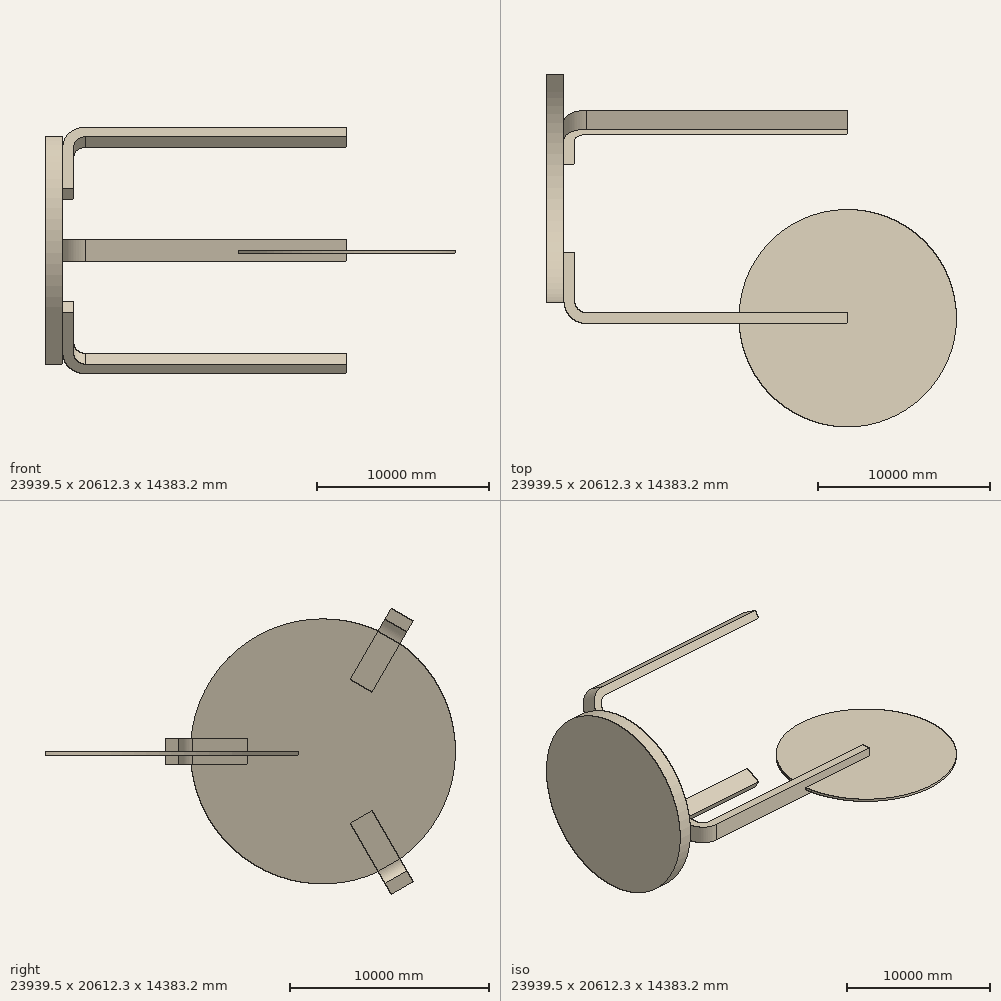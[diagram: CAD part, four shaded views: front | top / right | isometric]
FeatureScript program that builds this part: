
annotation { "Feature Type Name" : "Feature", "Feature Type Description" : "" }
export const myFeature = defineFeature(function(context is Context, id is Id, definition is map)
    precondition{}
    {
        {
            var Q0;
            Q0=qCreatedBy(makeId("Top.planeOp"),FACE);
            var sketch = newSketch(context, id + "F0", { "sketchPlane" : qUnion([Q0])});
            skCircle(sketch, "E0", {"center": v(0, 0) * mm, "radius": 6350 * mm});
            skSolve(sketch);
        }
        {
            var Q0;
            Q0 = qSketchRegion(id + "F0", true);
            extrude(context, id + "F1", {"entities" : qUnion([Q0]), "oppositeDirection" : true, "depth" : 177.8 * mm, "offsetDistance" : 25.4 * mm});
        }
        {
            var Q0;
            Q0=makeQuery(id+"F1.opExtrude","CAP_EDGE",EDGE,{"disambiguationData":[OSD([sQuery(id+"F0.wireOp",EDGE,"E0")])],"isStart":true});
            cPlane(context, id + "F2", {"entities" : qUnion([Q0]), "cplaneType" : CPlaneType.LINE_ANGLE, "offset" : 25.4 * mm, "angle" : 0 * degree, "width" : 152.4 * mm, "height" : 152.4 * mm});
        }
        {
            var Q0;
            Q0=qCreatedBy(id+"F2.planeOp",FACE);
            var sketch = newSketch(context, id + "F3", { "sketchPlane" : qUnion([Q0])});
            skLineSegment(sketch, "E1.bottom", {"start": v(0, 0) * mm, "end": v(1270, 0) * mm});
            skLineSegment(sketch, "E1.top", {"start": v(0, 508) * mm, "end": v(1270, 508) * mm});
            skLineSegment(sketch, "E1.left", {"start": v(0, 0) * mm, "end": v(0, 508) * mm});
            skLineSegment(sketch, "E1.right", {"start": v(1270, 0) * mm, "end": v(1270, 508) * mm});
            skSolve(sketch);
        }
        {
            var Q0;
            Q0=sQuery(id+"F3.wireOp",EDGE,"E1.bottom");
            cPlane(context, id + "F4", {"entities" : qUnion([Q0]), "cplaneType" : CPlaneType.LINE_ANGLE, "offset" : 25.4 * mm, "angle" : 0 * degree, "width" : 152.4 * mm, "height" : 152.4 * mm});
        }
        {
            var Q0;
            Q0=qCreatedBy(id+"F4.planeOp",FACE);
            var sketch = newSketch(context, id + "F5", { "sketchPlane" : qUnion([Q0])});
            skLineSegment(sketch, "E2", {"start": v(0, 0) * mm, "end": v(-15240, 0) * mm});
            skLineSegment(sketch, "E3", {"start": v(-16256, 1016) * mm, "end": v(-16256, 3810) * mm});
            skPoint(sketch, "E4.visualSharp", {"position": v(-16256, 0) * mm});
            skArc(sketch, "E4.filletArc", {"start": v(-16256, 1016) * mm, "mid": v(-15958.42, 297.58) * mm, "end": v(-15240, 0) * mm});
            skSolve(sketch);
        }
        {
            var Q0;
            Q0=qCreatedBy(id+"F2.planeOp",FACE);
            var sketch = newSketch(context, id + "F6", { "sketchPlane" : qUnion([Q0])});
            skLineSegment(sketch, "E5.bottom", {"start": v(-317.5, 635) * mm, "end": v(317.5, 635) * mm});
            skLineSegment(sketch, "E5.top", {"start": v(-317.5, -635) * mm, "end": v(317.5, -635) * mm});
            skLineSegment(sketch, "E5.left", {"start": v(-317.5, 635) * mm, "end": v(-317.5, -635) * mm});
            skLineSegment(sketch, "E5.right", {"start": v(317.5, 635) * mm, "end": v(317.5, -635) * mm});
            skPoint(sketch, "E5.middle", {"position": v(0, 0) * mm});
            skSolve(sketch);
        }
        {
            var Q0;
            Q0 = qSketchRegion(id + "F6", true);
            var Q1;
            Q1=sQuery(id+"F5.wireOp",EDGE,"E2");
            var Q2;
            Q2=sQuery(id+"F5.wireOp",EDGE,"E4.filletArc");
            var Q3;
            Q3=sQuery(id+"F5.wireOp",EDGE,"E3");
            sweep(context, id + "F7", {"profiles" : qUnion([Q0]), "path" : qUnion([Q1, Q2, Q3])});
        }
        {
            var Q0;
            Q0=makeQuery(id+"F7.opSweep","SWEPT_FACE",FACE,{"disambiguationData":[OSD([sQuery(id+"F5.wireOp",EDGE,"E3"),sQuery(id+"F6.wireOp",EDGE,"E5.left")])]});
            var Q1;
            Q1=makeQuery(id+"F7.opSweep","CAP_VERTEX",VERTEX,{"disambiguationData":[OSD([sQuery(id+"F5.wireOp",EDGE,"E3"),sQuery(id+"F6.wireOp",EDGE,"E5.top"),sQuery(id+"F6.wireOp",EDGE,"E5.left")])],"isStart":false});
            cPlane(context, id + "F8", {"entities" : qUnion([Q0, Q1]), "cplaneType" : CPlaneType.PLANE_POINT, "offset" : 25.4 * mm, "width" : 152.4 * mm, "height" : 152.4 * mm});
        }
        {
            var Q0;
            Q0=qCreatedBy(id+"F4.planeOp",FACE);
            var sketch = newSketch(context, id + "F9", { "sketchPlane" : qUnion([Q0])});
            skLineSegment(sketch, "E6", {"start": v(-14098.02, 7620) * mm, "end": v(0, 7620) * mm});
            skSolve(sketch);
        }
        {
            var Q0;
            Q0=makeQuery(id+"F7.opSweep","SWEPT_BODY",BODY,{"disambiguationData":[OSD([sQuery(id+"F5.wireOp",EDGE,"E3"),sQuery(id+"F6.wireOp",EDGE,"E5.bottom"),sQuery(id+"F6.wireOp",EDGE,"E5.top"),sQuery(id+"F6.wireOp",EDGE,"E5.left"),sQuery(id+"F6.wireOp",EDGE,"E5.right")])]});
            var Q1;
            Q1=sQuery(id+"F9.wireOp",EDGE,"E6");
            circularPattern(context, id + "F10", {"entities" : qUnion([Q0]), "axis" : qUnion([Q1]), "angle" : 360 * degree, "instanceCount" : 3, "equalSpace" : true});
        }
        {
            var Q0;
            Q0=makeQuery(id+"F7.opSweep","SWEPT_FACE",FACE,{"disambiguationData":[OSD([sQuery(id+"F5.wireOp",EDGE,"E3"),sQuery(id+"F6.wireOp",EDGE,"E5.left")])]});
            var Q1;
            Q1=makeQuery(id+"F7.opSweep","CAP_VERTEX",VERTEX,{"disambiguationData":[OSD([sQuery(id+"F5.wireOp",EDGE,"E3"),sQuery(id+"F6.wireOp",EDGE,"E5.bottom"),sQuery(id+"F6.wireOp",EDGE,"E5.left")])],"isStart":false});
            cPlane(context, id + "F11", {"entities" : qUnion([Q0, Q1]), "cplaneType" : CPlaneType.PLANE_POINT, "offset" : 25.4 * mm, "width" : 152.4 * mm, "height" : 152.4 * mm});
        }
        {
            var Q0;
            Q0=qCreatedBy(id+"F11.planeOp",FACE);
            var sketch = newSketch(context, id + "F12", { "sketchPlane" : qUnion([Q0])});
            skCircle(sketch, "E7", {"center": v(-7598.38, 5.23) * mm, "radius": 6663.95 * mm});
            skPoint(sketch, "E7.first.point", {"position": v(-965.8, -640.6) * mm});
            skPoint(sketch, "E7.second.point", {"position": v(-11470.7, -5418.18) * mm});
            skPoint(sketch, "E7.third.point", {"position": v(-11512.96, 5398.22) * mm});
            skSolve(sketch);
        }
        {
            var Q0;
            Q0 = qSketchRegion(id + "F12", true);
            extrude(context, id + "F13", {"entities" : qUnion([Q0]), "operationType" : NewBodyOperationType.ADD, "depth" : 1016 * mm, "offsetDistance" : 25.4 * mm});
        }
    });
